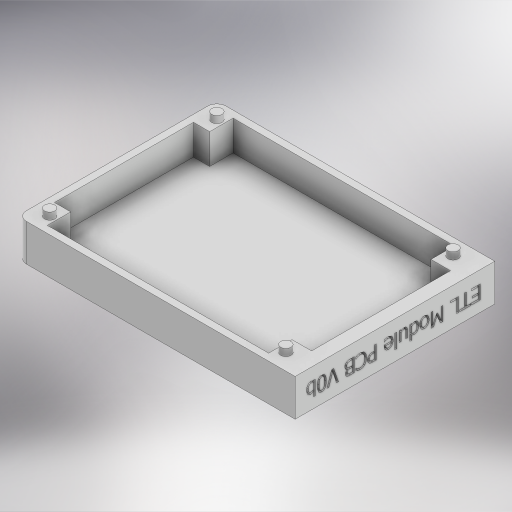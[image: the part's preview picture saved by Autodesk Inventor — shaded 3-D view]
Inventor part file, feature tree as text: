
AUTODESK INVENTOR PART (.ipt)
format: ipt  version: 2024 (Build 280153000, 153)  size: 680,448 bytes
history: native  units: in
note: dims shown in document units (in); Inventor stores cm internally (conversion verified against a paired STEP export)
features: sketch x4, extrude x3, fillet x1, emboss x1
ambient origin geometry x8: Origin, YZ Plane, XZ Plane, XY Plane, X Axis, Y Axis, Z Axis, Center Point
bodies: Solid1 (feature_tree)
feature tree (9):
  extrude  "Extrusion1"  Depth=2.3622in
  extrude  "Extrusion2"  Depth=0.0591in
  fillet  "Fillet1"  Radius=0.2559in
  extrude  "Extrusion3"  Depth=0.1969in
  emboss  "Emboss1"
  sketch  "Sketch1"  dims[d0=1.6969in d1=2.3622in]
  sketch  "Sketch2"  dims[d2=0.315in d3=0.0in d4=0.0591in d5=0.2559in d6=0.0in]
  sketch  "Sketch3"  dims[d7=0.2843in d8=0.1969in]
  sketch  "Sketch4"  dims[d9=0.0591in d10=0.0787in d11=0.0866in d12=0.0866in d13=0.2165in d14=0.0866in d15=0.0866in d16=2.2244in d17=0.0591in d18=0.0in d19=0.0394in d20=0.0in d21=1.4213in d22=0.1378in d23=1.6969in d24=1.1811in d25=0.5906in d26=0.1181in d27=1.1811in d28=0.0591in d29=0.5906in]
